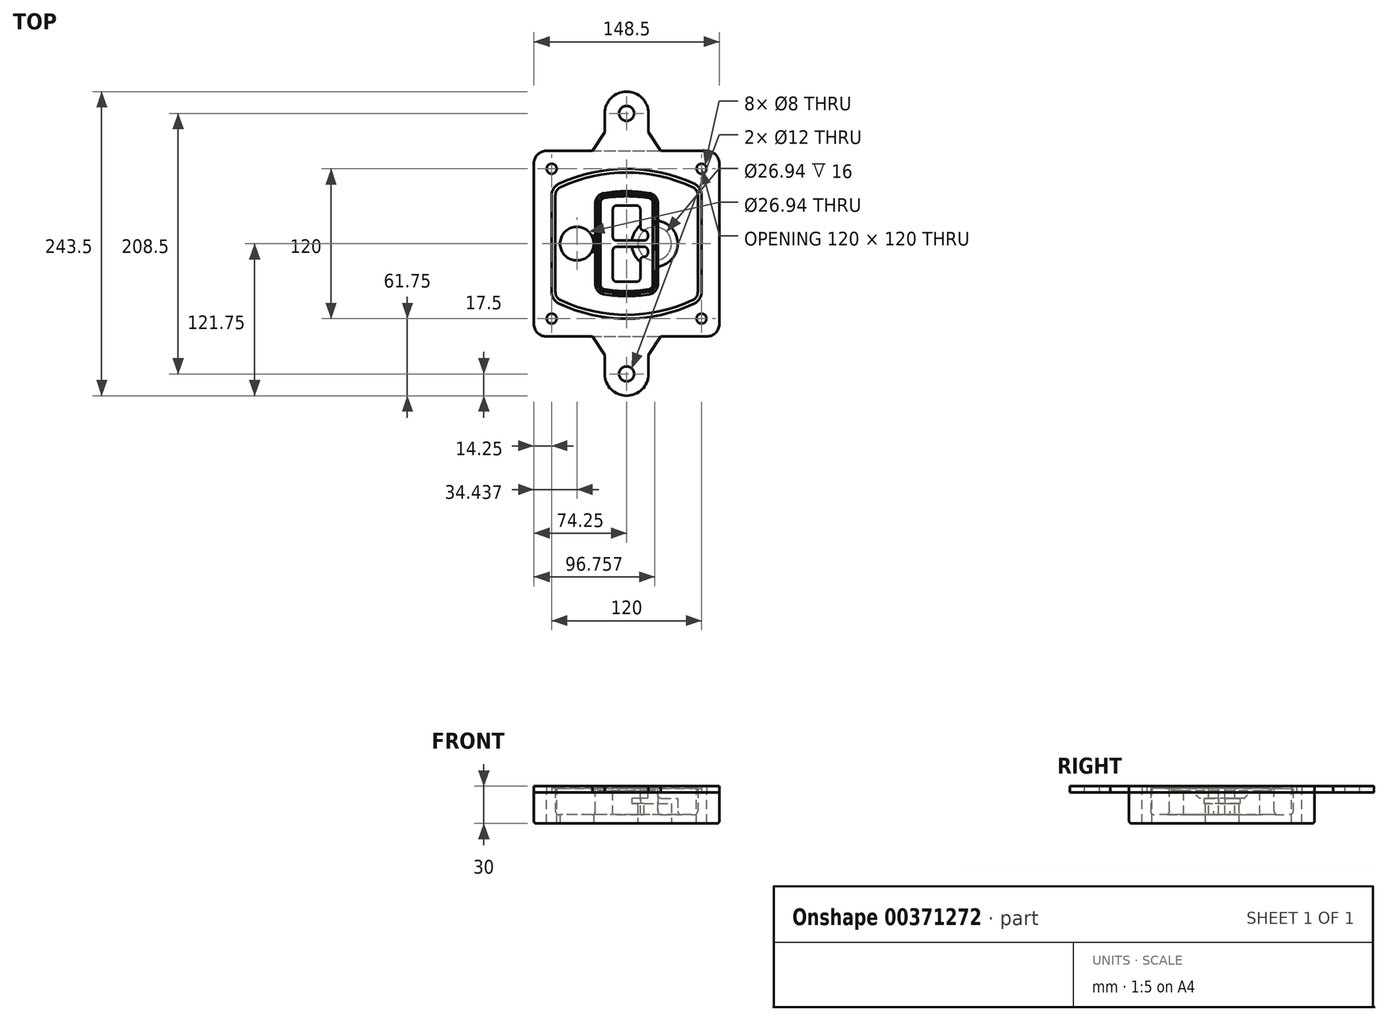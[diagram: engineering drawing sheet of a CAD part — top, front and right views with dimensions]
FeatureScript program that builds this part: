
annotation { "Feature Type Name" : "Feature", "Feature Type Description" : "" }
export const myFeature = defineFeature(function(context is Context, id is Id, definition is map)
    precondition{}
    {
        {
            var Q0;
            Q0=qCreatedBy(makeId("Top.planeOp"),FACE);
            var sketch = newSketch(context, id + "F0", { "sketchPlane" : qUnion([Q0])});
            skPoint(sketch, "E0.rect.middle", {"position": v(0, 0) * mm});
            skLineSegment(sketch, "E1.bottom", {"start": v(-64.25, -74.25) * mm, "end": v(64.25, -74.25) * mm});
            skLineSegment(sketch, "E1.top", {"start": v(-64.25, 74.25) * mm, "end": v(64.25, 74.25) * mm});
            skLineSegment(sketch, "E1.left", {"start": v(-74.25, -64.25) * mm, "end": v(-74.25, 64.25) * mm});
            skLineSegment(sketch, "E1.right", {"start": v(74.25, -64.25) * mm, "end": v(74.25, 64.25) * mm});
            skLineSegment(sketch, "E2", {"start": v(-74.25, 74.25) * mm, "end": v(74.25, -74.25) * mm, "construction": true});
            skLineSegment(sketch, "E3", {"start": v(74.25, 74.25) * mm, "end": v(-74.25, -74.25) * mm, "construction": true});
            skCircle(sketch, "E4", {"center": v(-60, 60) * mm, "radius": 4 * mm});
            skCircle(sketch, "E5", {"center": v(60, 60) * mm, "radius": 4 * mm});
            skCircle(sketch, "E6", {"center": v(60, -60) * mm, "radius": 4 * mm});
            skCircle(sketch, "E7", {"center": v(-60, -60) * mm, "radius": 4 * mm});
            skLineSegment(sketch, "E8", {"start": v(-60, 60) * mm, "end": v(60, 60) * mm, "construction": true});
            skLineSegment(sketch, "E9", {"start": v(60, 60) * mm, "end": v(60, -60) * mm, "construction": true});
            skLineSegment(sketch, "E10", {"start": v(60, -60) * mm, "end": v(-60, -60) * mm, "construction": true});
            skLineSegment(sketch, "E11", {"start": v(-60, -60) * mm, "end": v(-60, 60) * mm, "construction": true});
            skLineSegment(sketch, "E12", {"start": v(-60, 38.83) * mm, "end": v(-60, -38.83) * mm});
            skLineSegment(sketch, "E13", {"start": v(60, 38.83) * mm, "end": v(60, -38.83) * mm});
            skArc(sketch, "E14", {"start": v(54.26, 47.88) * mm, "mid": v(0, 60) * mm, "end": v(-54.26, 47.88) * mm});
            skArc(sketch, "E15", {"start": v(-54.26, -47.88) * mm, "mid": v(0, -60) * mm, "end": v(54.26, -47.88) * mm});
            skLineSegment(sketch, "E16", {"start": v(-60, 0) * mm, "end": v(60, 0) * mm, "construction": true});
            skPoint(sketch, "E17.visualSharp", {"position": v(-60, -45) * mm});
            skArc(sketch, "E17.filletArc", {"start": v(-60, -38.83) * mm, "mid": v(-58.44, -44.2) * mm, "end": v(-54.26, -47.88) * mm});
            skPoint(sketch, "E18.visualSharp", {"position": v(-60, 45) * mm});
            skArc(sketch, "E18.filletArc", {"start": v(-54.26, 47.88) * mm, "mid": v(-58.44, 44.2) * mm, "end": v(-60, 38.83) * mm});
            skPoint(sketch, "E19.visualSharp", {"position": v(60, 45) * mm});
            skArc(sketch, "E19.filletArc", {"start": v(60, 38.83) * mm, "mid": v(58.44, 44.2) * mm, "end": v(54.26, 47.88) * mm});
            skPoint(sketch, "E20.visualSharp", {"position": v(60, -45) * mm});
            skArc(sketch, "E20.filletArc", {"start": v(54.26, -47.88) * mm, "mid": v(58.44, -44.2) * mm, "end": v(60, -38.83) * mm});
            skPoint(sketch, "E21.visualSharp", {"position": v(-74.25, 74.25) * mm});
            skArc(sketch, "E21.filletArc", {"start": v(-64.25, 74.25) * mm, "mid": v(-71.32, 71.32) * mm, "end": v(-74.25, 64.25) * mm});
            skPoint(sketch, "E22.visualSharp", {"position": v(74.25, 74.25) * mm});
            skArc(sketch, "E22.filletArc", {"start": v(74.25, 64.25) * mm, "mid": v(71.32, 71.32) * mm, "end": v(64.25, 74.25) * mm});
            skPoint(sketch, "E23.visualSharp", {"position": v(74.25, -74.25) * mm});
            skArc(sketch, "E23.filletArc", {"start": v(64.25, -74.25) * mm, "mid": v(71.32, -71.32) * mm, "end": v(74.25, -64.25) * mm});
            skPoint(sketch, "E24.visualSharp", {"position": v(-74.25, -74.25) * mm});
            skArc(sketch, "E24.filletArc", {"start": v(-74.25, -64.25) * mm, "mid": v(-71.32, -71.32) * mm, "end": v(-64.25, -74.25) * mm});
            skArc(sketch, "E25.0", {"start": v(57, 38.83) * mm, "mid": v(55.9, 42.58) * mm, "end": v(52.98, 45.17) * mm});
            skLineSegment(sketch, "E25.1", {"start": v(57, 38.83) * mm, "end": v(57, -38.83) * mm});
            skArc(sketch, "E25.2", {"start": v(52.98, -45.17) * mm, "mid": v(55.9, -42.58) * mm, "end": v(57, -38.83) * mm});
            skArc(sketch, "E25.3", {"start": v(-52.98, -45.17) * mm, "mid": v(0, -57) * mm, "end": v(52.98, -45.17) * mm});
            skArc(sketch, "E25.4", {"start": v(-57, -38.83) * mm, "mid": v(-55.9, -42.58) * mm, "end": v(-52.98, -45.17) * mm});
            skArc(sketch, "E25.5", {"start": v(52.98, 45.17) * mm, "mid": v(0, 57) * mm, "end": v(-52.98, 45.17) * mm});
            skLineSegment(sketch, "E25.6", {"start": v(-57, 38.83) * mm, "end": v(-57, -38.83) * mm});
            skArc(sketch, "E25.7", {"start": v(-52.98, 45.17) * mm, "mid": v(-55.9, 42.58) * mm, "end": v(-57, 38.83) * mm});
            skArc(sketch, "E26.0", {"start": v(-55.96, 51.5) * mm, "mid": v(-61.82, 46.33) * mm, "end": v(-64, 38.83) * mm});
            skArc(sketch, "E26.1", {"start": v(55.96, 51.5) * mm, "mid": v(0, 64) * mm, "end": v(-55.96, 51.5) * mm});
            skArc(sketch, "E26.2", {"start": v(64, 38.83) * mm, "mid": v(61.82, 46.33) * mm, "end": v(55.96, 51.5) * mm});
            skLineSegment(sketch, "E26.3", {"start": v(64, 38.83) * mm, "end": v(64, -38.83) * mm});
            skArc(sketch, "E26.4", {"start": v(55.96, -51.5) * mm, "mid": v(61.82, -46.33) * mm, "end": v(64, -38.83) * mm});
            skLineSegment(sketch, "E26.5", {"start": v(-64, 38.83) * mm, "end": v(-64, -38.83) * mm});
            skArc(sketch, "E26.6", {"start": v(-55.96, -51.5) * mm, "mid": v(0, -64) * mm, "end": v(55.96, -51.5) * mm});
            skArc(sketch, "E26.7", {"start": v(-64, -38.83) * mm, "mid": v(-61.82, -46.33) * mm, "end": v(-55.96, -51.5) * mm});
            skSolve(sketch);
        }
        {
            var Q0;
            Q0=makeQuery(id+"F0.imprint","IMPRINT",FACE,{"disambiguationData":[TD([[makeQuery(id+"F0.imprint","IMPRINT",EDGE,{"derivedFrom":sQuery(id+"F0.wireOp",EDGE,"E1.bottom")}),1.0]])]});
            var Q1;
            Q1=makeQuery(id+"F0.imprint","IMPRINT",FACE,{"disambiguationData":[TD([[makeQuery(id+"F0.imprint","IMPRINT",EDGE,{"derivedFrom":sQuery(id+"F0.wireOp",EDGE,"E12")}),1.0]])]});
            var Q2;
            Q2=makeQuery(id+"F0.imprint","IMPRINT",FACE,{"disambiguationData":[TD([[makeQuery(id+"F0.imprint","IMPRINT",EDGE,{"derivedFrom":sQuery(id+"F0.wireOp",EDGE,"E25.0")}),1.0]])]});
            var Q3;
            Q3=makeQuery(id+"F0.imprint","IMPRINT",FACE,{"disambiguationData":[TD([[makeQuery(id+"F0.imprint","IMPRINT",EDGE,{"derivedFrom":sQuery(id+"F0.wireOp",EDGE,"E12")}),-1.0]])]});
            extrude(context, id + "F1", {"entities" : qUnion([Q0, Q1, Q2, Q3]), "oppositeDirection" : true, "depth" : 25 * mm});
        }
        {
            var Q0;
            Q0=makeQuery(id+"F0.imprint","IMPRINT",FACE,{"disambiguationData":[TD([[makeQuery(id+"F0.imprint","IMPRINT",EDGE,{"derivedFrom":sQuery(id+"F0.wireOp",EDGE,"E12")}),1.0]])]});
            extrude(context, id + "F2", {"entities" : qUnion([Q0]), "operationType" : NewBodyOperationType.ADD, "depth" : 3 * mm});
        }
        {
            var Q0;
            Q0=makeQuery(id+"F0.imprint","IMPRINT",FACE,{"disambiguationData":[TD([[makeQuery(id+"F0.imprint","IMPRINT",EDGE,{"derivedFrom":sQuery(id+"F0.wireOp",EDGE,"E25.0")}),1.0]])]});
            extrude(context, id + "F3", {"entities" : qUnion([Q0]), "operationType" : NewBodyOperationType.REMOVE, "oppositeDirection" : true, "depth" : 18 * mm});
        }
        {
            var Q0;
            Q0=makeQuery(id+"F2.opExtrude","CAP_FACE",FACE,{"disambiguationData":[OSD([sQuery(id+"F0.wireOp",EDGE,"E12"),sQuery(id+"F0.wireOp",EDGE,"E13"),sQuery(id+"F0.wireOp",EDGE,"E14"),sQuery(id+"F0.wireOp",EDGE,"E15"),sQuery(id+"F0.wireOp",EDGE,"E17.filletArc"),sQuery(id+"F0.wireOp",EDGE,"E18.filletArc"),sQuery(id+"F0.wireOp",EDGE,"E19.filletArc"),sQuery(id+"F0.wireOp",EDGE,"E20.filletArc"),sQuery(id+"F0.wireOp",EDGE,"E25.0"),sQuery(id+"F0.wireOp",EDGE,"E25.1"),sQuery(id+"F0.wireOp",EDGE,"E25.2"),sQuery(id+"F0.wireOp",EDGE,"E25.3"),sQuery(id+"F0.wireOp",EDGE,"E25.4"),sQuery(id+"F0.wireOp",EDGE,"E25.5"),sQuery(id+"F0.wireOp",EDGE,"E25.6"),sQuery(id+"F0.wireOp",EDGE,"E25.7")])],"isStart":false});
            var sketch = newSketch(context, id + "F4", { "sketchPlane" : qUnion([Q0])});
            skArc(sketch, "E27.0", {"start": v(-18.34, -40.45) * mm, "mid": v(0, -42) * mm, "end": v(18.34, -40.45) * mm});
            skArc(sketch, "E28.0", {"start": v(18.34, 40.45) * mm, "mid": v(0, 42) * mm, "end": v(-18.34, 40.45) * mm});
            skLineSegment(sketch, "E29", {"start": v(-25, 32.57) * mm, "end": v(-25, -32.57) * mm});
            skLineSegment(sketch, "E30", {"start": v(25, 32.57) * mm, "end": v(25, -32.57) * mm});
            skLineSegment(sketch, "E31", {"start": v(-25, 39.1) * mm, "end": v(25, 39.1) * mm, "construction": true});
            skLineSegment(sketch, "E32", {"start": v(-25, -39.1) * mm, "end": v(25, -39.1) * mm, "construction": true});
            skPoint(sketch, "E33.visualSharp", {"position": v(-25, 39.1) * mm});
            skArc(sketch, "E33.filletArc", {"start": v(-18.34, 40.45) * mm, "mid": v(-23.11, 37.73) * mm, "end": v(-25, 32.57) * mm});
            skPoint(sketch, "E34.visualSharp", {"position": v(25, 39.1) * mm});
            skArc(sketch, "E34.filletArc", {"start": v(25, 32.57) * mm, "mid": v(23.11, 37.73) * mm, "end": v(18.34, 40.45) * mm});
            skPoint(sketch, "E35.visualSharp", {"position": v(25, -39.1) * mm});
            skArc(sketch, "E35.filletArc", {"start": v(18.34, -40.45) * mm, "mid": v(23.11, -37.73) * mm, "end": v(25, -32.57) * mm});
            skPoint(sketch, "E36.visualSharp", {"position": v(-25, -39.1) * mm});
            skArc(sketch, "E36.filletArc", {"start": v(-25, -32.57) * mm, "mid": v(-23.11, -37.73) * mm, "end": v(-18.34, -40.45) * mm});
            skArc(sketch, "E37.0", {"start": v(52.98, 45.17) * mm, "mid": v(0, 57) * mm, "end": v(-52.98, 45.17) * mm});
            skArc(sketch, "E37.1", {"start": v(-52.98, 45.17) * mm, "mid": v(-55.9, 42.58) * mm, "end": v(-57, 38.83) * mm});
            skLineSegment(sketch, "E37.2", {"start": v(-57, 38.83) * mm, "end": v(-57, -38.83) * mm});
            skArc(sketch, "E37.3", {"start": v(-57, -38.83) * mm, "mid": v(-55.9, -42.58) * mm, "end": v(-52.98, -45.17) * mm});
            skArc(sketch, "E37.4", {"start": v(-52.98, -45.17) * mm, "mid": v(0, -57) * mm, "end": v(52.98, -45.17) * mm});
            skArc(sketch, "E37.5", {"start": v(52.98, -45.17) * mm, "mid": v(55.9, -42.58) * mm, "end": v(57, -38.83) * mm});
            skLineSegment(sketch, "E37.6", {"start": v(57, 38.83) * mm, "end": v(57, -38.83) * mm});
            skArc(sketch, "E37.7", {"start": v(57, 38.83) * mm, "mid": v(55.9, 42.58) * mm, "end": v(52.98, 45.17) * mm});
            skLineSegment(sketch, "E38.0", {"start": v(23, 32.57) * mm, "end": v(23, -32.57) * mm});
            skArc(sketch, "E38.1", {"start": v(18, -38.48) * mm, "mid": v(21.58, -36.44) * mm, "end": v(23, -32.57) * mm});
            skArc(sketch, "E38.2", {"start": v(-18, -38.48) * mm, "mid": v(0, -40) * mm, "end": v(18, -38.48) * mm});
            skArc(sketch, "E38.3", {"start": v(-23, -32.57) * mm, "mid": v(-21.58, -36.44) * mm, "end": v(-18, -38.48) * mm});
            skLineSegment(sketch, "E38.4", {"start": v(-23, 32.57) * mm, "end": v(-23, -32.57) * mm});
            skArc(sketch, "E38.5", {"start": v(23, 32.57) * mm, "mid": v(21.58, 36.44) * mm, "end": v(18, 38.48) * mm});
            skArc(sketch, "E38.6", {"start": v(-18, 38.48) * mm, "mid": v(-21.58, 36.44) * mm, "end": v(-23, 32.57) * mm});
            skArc(sketch, "E38.7", {"start": v(18, 38.48) * mm, "mid": v(0, 40) * mm, "end": v(-18, 38.48) * mm});
            skArc(sketch, "E39.0", {"start": v(21, 32.57) * mm, "mid": v(20.06, 35.15) * mm, "end": v(17.67, 36.5) * mm});
            skLineSegment(sketch, "E39.1", {"start": v(21, 32.57) * mm, "end": v(21, -32.57) * mm});
            skArc(sketch, "E39.2", {"start": v(17.67, -36.5) * mm, "mid": v(20.06, -35.15) * mm, "end": v(21, -32.57) * mm});
            skArc(sketch, "E39.3", {"start": v(-17.67, -36.5) * mm, "mid": v(0, -38) * mm, "end": v(17.67, -36.5) * mm});
            skArc(sketch, "E39.4", {"start": v(-21, -32.57) * mm, "mid": v(-20.06, -35.15) * mm, "end": v(-17.67, -36.5) * mm});
            skArc(sketch, "E39.5", {"start": v(17.67, 36.5) * mm, "mid": v(0, 38) * mm, "end": v(-17.67, 36.5) * mm});
            skLineSegment(sketch, "E39.6", {"start": v(-21, 32.57) * mm, "end": v(-21, -32.57) * mm});
            skArc(sketch, "E39.7", {"start": v(-17.67, 36.5) * mm, "mid": v(-20.06, 35.15) * mm, "end": v(-21, 32.57) * mm});
            skLineSegment(sketch, "E40", {"start": v(-25, 0) * mm, "end": v(25, 0) * mm, "construction": true});
            skLineSegment(sketch, "E41", {"start": v(-11, 5.5) * mm, "end": v(-11, 27.5) * mm});
            skLineSegment(sketch, "E42", {"start": v(-8, 30.5) * mm, "end": v(8, 30.5) * mm});
            skLineSegment(sketch, "E43", {"start": v(11, 27.5) * mm, "end": v(11, 13.5) * mm});
            skLineSegment(sketch, "E44", {"start": v(14, 10.5) * mm, "end": v(14, 10.5) * mm});
            skLineSegment(sketch, "E45", {"start": v(17, 7.5) * mm, "end": v(17, 5.5) * mm});
            skLineSegment(sketch, "E46", {"start": v(14, 2.5) * mm, "end": v(-8, 2.5) * mm});
            skPoint(sketch, "E47.visualSharp", {"position": v(-11, 30.5) * mm});
            skArc(sketch, "E47.filletArc", {"start": v(-8, 30.5) * mm, "mid": v(-10.12, 29.62) * mm, "end": v(-11, 27.5) * mm});
            skPoint(sketch, "E48.visualSharp", {"position": v(11, 30.5) * mm});
            skArc(sketch, "E48.filletArc", {"start": v(11, 27.5) * mm, "mid": v(10.12, 29.62) * mm, "end": v(8, 30.5) * mm});
            skPoint(sketch, "E49.visualSharp", {"position": v(11, 10.5) * mm});
            skArc(sketch, "E49.filletArc", {"start": v(11, 13.5) * mm, "mid": v(11.88, 11.38) * mm, "end": v(14, 10.5) * mm});
            skPoint(sketch, "E50.visualSharp", {"position": v(17, 10.5) * mm});
            skArc(sketch, "E50.filletArc", {"start": v(17, 7.5) * mm, "mid": v(16.12, 9.62) * mm, "end": v(14, 10.5) * mm});
            skPoint(sketch, "E51.visualSharp", {"position": v(17, 2.5) * mm});
            skArc(sketch, "E51.filletArc", {"start": v(14, 2.5) * mm, "mid": v(16.12, 3.38) * mm, "end": v(17, 5.5) * mm});
            skPoint(sketch, "E52.visualSharp", {"position": v(-11, 2.5) * mm});
            skArc(sketch, "E52.filletArc", {"start": v(-11, 5.5) * mm, "mid": v(-10.12, 3.38) * mm, "end": v(-8, 2.5) * mm});
            skLineSegment(sketch, "E53.0.MirrorCS", {"start": v(14, -2.5) * mm, "end": v(-8, -2.5) * mm});
            skArc(sketch, "E54.0.MirrorCS", {"start": v(-11, -5.5) * mm, "mid": v(-10.12, -3.38) * mm, "end": v(-8, -2.5) * mm});
            skLineSegment(sketch, "E55.0.MirrorCS", {"start": v(-11, -5.5) * mm, "end": v(-11, -27.5) * mm});
            skArc(sketch, "E56.0.MirrorCS", {"start": v(-8, -30.5) * mm, "mid": v(-10.12, -29.62) * mm, "end": v(-11, -27.5) * mm});
            skLineSegment(sketch, "E57.0.MirrorCS", {"start": v(-8, -30.5) * mm, "end": v(8, -30.5) * mm});
            skArc(sketch, "E58.0.MirrorCS", {"start": v(11, -27.5) * mm, "mid": v(10.12, -29.62) * mm, "end": v(8, -30.5) * mm});
            skLineSegment(sketch, "E59.0.MirrorCS", {"start": v(11, -27.5) * mm, "end": v(11, -13.5) * mm});
            skArc(sketch, "E60.0.MirrorCS", {"start": v(11, -13.5) * mm, "mid": v(11.88, -11.38) * mm, "end": v(14, -10.5) * mm});
            skArc(sketch, "E61.0.MirrorCS", {"start": v(17, -7.5) * mm, "mid": v(16.12, -9.62) * mm, "end": v(14, -10.5) * mm});
            skLineSegment(sketch, "E62.0.MirrorCS", {"start": v(17, -7.5) * mm, "end": v(17, -5.5) * mm});
            skArc(sketch, "E63.0.MirrorCS", {"start": v(14, -2.5) * mm, "mid": v(16.12, -3.38) * mm, "end": v(17, -5.5) * mm});
            skSolve(sketch);
        }
        {
            var Q0;
            Q0=makeQuery(id+"F4.imprint","IMPRINT",FACE,{"disambiguationData":[TD([[makeQuery(id+"F4.imprint","IMPRINT",EDGE,{"derivedFrom":sQuery(id+"F4.wireOp",EDGE,"E27.0")}),1.0]])]});
            var Q1;
            Q1=makeQuery(id+"F4.imprint","IMPRINT",FACE,{"disambiguationData":[TD([[makeQuery(id+"F4.imprint","IMPRINT",EDGE,{"derivedFrom":sQuery(id+"F4.wireOp",EDGE,"E38.0")}),-1.0]])]});
            var Q2;
            Q2=makeQuery(id+"F4.imprint","IMPRINT",FACE,{"disambiguationData":[TD([[makeQuery(id+"F4.imprint","IMPRINT",EDGE,{"derivedFrom":sQuery(id+"F4.wireOp",EDGE,"E39.0")}),1.0]])]});
            extrude(context, id + "F5", {"entities" : qUnion([Q0, Q1, Q2]), "operationType" : NewBodyOperationType.ADD, "endBound" : BoundingType.UP_TO_NEXT, "oppositeDirection" : true, "depth" : 25 * mm});
        }
        {
            var Q0;
            Q0=makeQuery(id+"F4.imprint","IMPRINT",FACE,{"disambiguationData":[TD([[makeQuery(id+"F4.imprint","IMPRINT",EDGE,{"derivedFrom":sQuery(id+"F4.wireOp",EDGE,"E38.0")}),-1.0]])]});
            extrude(context, id + "F6", {"entities" : qUnion([Q0]), "operationType" : NewBodyOperationType.REMOVE, "oppositeDirection" : true, "depth" : 2 * mm});
        }
        {
            var Q0;
            Q0=makeQuery(id+"F1.opExtrude","CAP_FACE",FACE,{"disambiguationData":[OSD([sQuery(id+"F0.wireOp",EDGE,"E1.bottom"),sQuery(id+"F0.wireOp",EDGE,"E1.top"),sQuery(id+"F0.wireOp",EDGE,"E1.left"),sQuery(id+"F0.wireOp",EDGE,"E1.right"),sQuery(id+"F0.wireOp",EDGE,"E4"),sQuery(id+"F0.wireOp",EDGE,"E5"),sQuery(id+"F0.wireOp",EDGE,"E6"),sQuery(id+"F0.wireOp",EDGE,"E7"),sQuery(id+"F0.wireOp",EDGE,"E21.filletArc"),sQuery(id+"F0.wireOp",EDGE,"E22.filletArc"),sQuery(id+"F0.wireOp",EDGE,"E23.filletArc"),sQuery(id+"F0.wireOp",EDGE,"E24.filletArc")])],"isStart":false});
            var sketch = newSketch(context, id + "F7", { "sketchPlane" : qUnion([Q0])});
            skCircle(sketch, "E64", {"center": v(22.5, 0) * mm, "radius": 13.47 * mm});
            skCircle(sketch, "E65", {"center": v(-39.81, 0) * mm, "radius": 13.47 * mm});
            skLineSegment(sketch, "E66", {"start": v(74.25, 0) * mm, "end": v(-74.25, 0) * mm});
            skCircle(sketch, "E67", {"center": v(22.5, 0) * mm, "radius": 18.47 * mm});
            skCircle(sketch, "E68", {"center": v(60, -60) * mm, "radius": 6 * mm});
            skCircle(sketch, "E69", {"center": v(-60, -60) * mm, "radius": 6 * mm});
            skCircle(sketch, "E70", {"center": v(-60, 60) * mm, "radius": 6 * mm});
            skCircle(sketch, "E71", {"center": v(60, 60) * mm, "radius": 6 * mm});
            skSolve(sketch);
        }
        {
            var Q0;
            {var subQ1=sQuery(id+"F7.wireOp",EDGE,"E66");var subQ4=sQuery(id+"F7.wireOp",EDGE,"E64");var subQ6=makeQuery(id+"F7.imprint","INTERSECT",VERTEX,{"disambiguationData":[OD(0.0)],"derivedFrom":[subQ4,subQ1]});Q0=makeQuery(id+"F7.imprint","IMPRINT",FACE,{"disambiguationData":[TD([[makeQuery(id+"F7.imprint","IMPRINT",EDGE,{"disambiguationData":[TD([[subQ6,-1.0]])],"derivedFrom":subQ4}),-1.0]])]});}
            var Q1;
            {var subQ0=sQuery(id+"F7.wireOp",EDGE,"E66");var subQ1=sQuery(id+"F7.wireOp",EDGE,"E64");var subQ3=makeQuery(id+"F7.imprint","INTERSECT",VERTEX,{"disambiguationData":[OD(0.0)],"derivedFrom":[subQ1,subQ0]});Q1=makeQuery(id+"F7.imprint","IMPRINT",FACE,{"disambiguationData":[TD([[makeQuery(id+"F7.imprint","IMPRINT",EDGE,{"disambiguationData":[TD([[subQ3,-1.0]])],"derivedFrom":subQ1}),1.0]])]});}
            var Q2;
            {var subQ0=sQuery(id+"F7.wireOp",EDGE,"E66");var subQ1=sQuery(id+"F7.wireOp",EDGE,"E64");var subQ3=makeQuery(id+"F7.imprint","INTERSECT",VERTEX,{"disambiguationData":[OD(0.0)],"derivedFrom":[subQ1,subQ0]});Q2=makeQuery(id+"F7.imprint","IMPRINT",FACE,{"disambiguationData":[TD([[makeQuery(id+"F7.imprint","IMPRINT",EDGE,{"disambiguationData":[TD([[subQ3,1.0]])],"derivedFrom":subQ1}),1.0]])]});}
            var Q3;
            {var subQ1=sQuery(id+"F7.wireOp",EDGE,"E66");var subQ4=sQuery(id+"F7.wireOp",EDGE,"E64");var subQ6=makeQuery(id+"F7.imprint","INTERSECT",VERTEX,{"disambiguationData":[OD(0.0)],"derivedFrom":[subQ4,subQ1]});Q3=makeQuery(id+"F7.imprint","IMPRINT",FACE,{"disambiguationData":[TD([[makeQuery(id+"F7.imprint","IMPRINT",EDGE,{"disambiguationData":[TD([[subQ6,1.0]])],"derivedFrom":subQ4}),-1.0]])]});}
            extrude(context, id + "F8", {"entities" : qUnion([Q0, Q1, Q2, Q3]), "operationType" : NewBodyOperationType.ADD, "oppositeDirection" : true, "depth" : 20 * mm});
        }
        {
            var Q0;
            {var subQ0=sQuery(id+"F7.wireOp",EDGE,"E66");var subQ1=sQuery(id+"F7.wireOp",EDGE,"E64");var subQ3=makeQuery(id+"F7.imprint","INTERSECT",VERTEX,{"disambiguationData":[OD(0.0)],"derivedFrom":[subQ1,subQ0]});Q0=makeQuery(id+"F7.imprint","IMPRINT",FACE,{"disambiguationData":[TD([[makeQuery(id+"F7.imprint","IMPRINT",EDGE,{"disambiguationData":[TD([[subQ3,-1.0]])],"derivedFrom":subQ1}),1.0]])]});}
            var Q1;
            {var subQ0=sQuery(id+"F7.wireOp",EDGE,"E66");var subQ1=sQuery(id+"F7.wireOp",EDGE,"E64");var subQ3=makeQuery(id+"F7.imprint","INTERSECT",VERTEX,{"disambiguationData":[OD(0.0)],"derivedFrom":[subQ1,subQ0]});Q1=makeQuery(id+"F7.imprint","IMPRINT",FACE,{"disambiguationData":[TD([[makeQuery(id+"F7.imprint","IMPRINT",EDGE,{"disambiguationData":[TD([[subQ3,1.0]])],"derivedFrom":subQ1}),1.0]])]});}
            extrude(context, id + "F9", {"entities" : qUnion([Q0, Q1]), "operationType" : NewBodyOperationType.REMOVE, "oppositeDirection" : true, "depth" : 16 * mm});
        }
        {
            var Q0;
            {var subQ0=sQuery(id+"F7.wireOp",EDGE,"E66");var subQ1=sQuery(id+"F7.wireOp",EDGE,"E65");var subQ3=makeQuery(id+"F7.imprint","INTERSECT",VERTEX,{"disambiguationData":[OD(0.0)],"derivedFrom":[subQ1,subQ0]});Q0=makeQuery(id+"F7.imprint","IMPRINT",FACE,{"disambiguationData":[TD([[makeQuery(id+"F7.imprint","IMPRINT",EDGE,{"disambiguationData":[TD([[subQ3,-1.0]])],"derivedFrom":subQ1}),1.0]])]});}
            var Q1;
            {var subQ0=sQuery(id+"F7.wireOp",EDGE,"E66");var subQ1=sQuery(id+"F7.wireOp",EDGE,"E65");var subQ3=makeQuery(id+"F7.imprint","INTERSECT",VERTEX,{"disambiguationData":[OD(0.0)],"derivedFrom":[subQ1,subQ0]});Q1=makeQuery(id+"F7.imprint","IMPRINT",FACE,{"disambiguationData":[TD([[makeQuery(id+"F7.imprint","IMPRINT",EDGE,{"disambiguationData":[TD([[subQ3,1.0]])],"derivedFrom":subQ1}),1.0]])]});}
            extrude(context, id + "F10", {"entities" : qUnion([Q0, Q1]), "operationType" : NewBodyOperationType.REMOVE, "oppositeDirection" : true, "depth" : 25 * mm});
        }
        {
            var Q0;
            Q0=makeQuery(id+"F9.boolean.opBoolean","COPY",FACE,{"derivedFrom":makeQuery(id+"F9.opExtrude","CAP_FACE",FACE,{"disambiguationData":[OSD([sQuery(id+"F7.wireOp",EDGE,"E64")])],"isStart":false})});
            var sketch = newSketch(context, id + "F11", { "sketchPlane" : qUnion([Q0])});
            skArc(sketch, "E72.0", {"start": v(11, 14.45) * mm, "mid": v(6.45, 9.13) * mm, "end": v(4.2, 2.5) * mm});
            skArc(sketch, "E72.1", {"start": v(4.2, -2.5) * mm, "mid": v(6.45, -9.13) * mm, "end": v(11, -14.45) * mm});
            skLineSegment(sketch, "E73", {"start": v(4.2, -2.5) * mm, "end": v(14, -2.5) * mm});
            skLineSegment(sketch, "E74.0", {"start": v(14, 2.5) * mm, "end": v(4.2, 2.5) * mm});
            skArc(sketch, "E74.1", {"start": v(14, 2.5) * mm, "mid": v(16.12, 3.38) * mm, "end": v(17, 5.5) * mm});
            skLineSegment(sketch, "E74.2", {"start": v(17, 7.5) * mm, "end": v(17, 5.5) * mm});
            skArc(sketch, "E74.3", {"start": v(17, 7.5) * mm, "mid": v(16.12, 9.62) * mm, "end": v(14, 10.5) * mm});
            skArc(sketch, "E74.4", {"start": v(11, 13.5) * mm, "mid": v(11.88, 11.38) * mm, "end": v(14, 10.5) * mm});
            skLineSegment(sketch, "E74.5", {"start": v(11, 14.45) * mm, "end": v(11, 13.5) * mm});
            skLineSegment(sketch, "E74.7", {"start": v(14, -2.5) * mm, "end": v(4.2, -2.5) * mm});
            skArc(sketch, "E74.8", {"start": v(14, -2.5) * mm, "mid": v(16.12, -3.38) * mm, "end": v(17, -5.5) * mm});
            skLineSegment(sketch, "E74.9", {"start": v(17, -7.5) * mm, "end": v(17, -5.5) * mm});
            skArc(sketch, "E74.10", {"start": v(17, -7.5) * mm, "mid": v(16.12, -9.62) * mm, "end": v(14, -10.5) * mm});
            skArc(sketch, "E74.11", {"start": v(11, -13.5) * mm, "mid": v(11.88, -11.38) * mm, "end": v(14, -10.5) * mm});
            skLineSegment(sketch, "E74.12", {"start": v(11, -14.45) * mm, "end": v(11, -13.5) * mm});
            skPoint(sketch, "E75.orphan", {"position": v(11, -27.5) * mm});
            skPoint(sketch, "E76.orphan", {"position": v(-8, -2.5) * mm});
            skPoint(sketch, "E77.orphan", {"position": v(-8, 2.5) * mm});
            skPoint(sketch, "E78.orphan", {"position": v(11, 27.5) * mm});
            skSolve(sketch);
        }
        {
            var Q0;
            {var subQ7=sQuery(id+"F11.wireOp",EDGE,"E72.0");var subQ14=sQuery(id+"F11.wireOp",EDGE,"E72.1");var subQ16=sQuery(id+"F11.wireOp",EDGE,"E74.1");var subQ18=sQuery(id+"F11.wireOp",EDGE,"E74.8");Q0=qUnion([makeQuery(id+"F11.imprint","IMPRINT",FACE,{"disambiguationData":[TD([[makeQuery(id+"F11.imprint","IMPRINT",EDGE,{"derivedFrom":subQ7}),1.0]])]}),makeQuery(id+"F11.imprint","IMPRINT",FACE,{"disambiguationData":[TD([[makeQuery(id+"F11.imprint","IMPRINT",EDGE,{"derivedFrom":subQ14}),1.0]])]}),makeQuery(id+"F11.imprint","IMPRINT",FACE,{"disambiguationData":[TD([[makeQuery(id+"F11.imprint","IMPRINT",EDGE,{"derivedFrom":subQ16}),1.0]])]}),makeQuery(id+"F11.imprint","IMPRINT",FACE,{"disambiguationData":[TD([[makeQuery(id+"F11.imprint","IMPRINT",EDGE,{"derivedFrom":subQ18}),-1.0]])]})]);}
            var Q1;
            Q1=makeQuery(id+"F5.boolean.opBoolean","SPLIT",FACE,{"disambiguationData":[TD([makeQuery(id+"F5.opExtrude","SWEPT_FACE",FACE,{"disambiguationData":[OSD([sQuery(id+"F4.wireOp",EDGE,"E41")])]})])],"derivedFrom":makeQuery(id+"F3.boolean.opBoolean","COPY",FACE,{"derivedFrom":makeQuery(id+"F3.opExtrude","CAP_FACE",FACE,{"disambiguationData":[OSD([sQuery(id+"F0.wireOp",EDGE,"E25.0"),sQuery(id+"F0.wireOp",EDGE,"E25.1"),sQuery(id+"F0.wireOp",EDGE,"E25.2"),sQuery(id+"F0.wireOp",EDGE,"E25.3"),sQuery(id+"F0.wireOp",EDGE,"E25.4"),sQuery(id+"F0.wireOp",EDGE,"E25.5"),sQuery(id+"F0.wireOp",EDGE,"E25.6"),sQuery(id+"F0.wireOp",EDGE,"E25.7")])],"isStart":false})})});
            extrude(context, id + "F12", {"entities" : qUnion([Q0]), "operationType" : NewBodyOperationType.REMOVE, "endBound" : BoundingType.UP_TO_SURFACE, "endBoundEntityFace" : qUnion([Q1]), "depth" : 25 * mm});
        }
        {
            var Q0;
            Q0=makeQuery(id+"F3.boolean.opBoolean","COPY",EDGE,{"derivedFrom":makeQuery(id+"F3.opExtrude","CAP_EDGE",EDGE,{"disambiguationData":[OSD([sQuery(id+"F0.wireOp",EDGE,"E25.6")])],"isStart":false})});
            var Q1;
            Q1=makeQuery(id+"F8.boolean.opBoolean","INTERSECT",EDGE,{"derivedFrom":[makeQuery(id+"F5.opExtrude","SWEPT_FACE",FACE,{"disambiguationData":[OSD([sQuery(id+"F4.wireOp",EDGE,"E30")])]}),makeQuery(id+"F8.opExtrude","CAP_FACE",FACE,{"disambiguationData":[OSD([sQuery(id+"F7.wireOp",EDGE,"E67")])],"isStart":false})]});
            var Q2;
            Q2=makeQuery(id+"F8.boolean.opBoolean","INTERSECT",EDGE,{"disambiguationData":[OD(1.0)],"derivedFrom":[makeQuery(id+"F5.opExtrude","SWEPT_FACE",FACE,{"disambiguationData":[OSD([sQuery(id+"F4.wireOp",EDGE,"E30")])]}),makeQuery(id+"F8.opExtrude","SWEPT_FACE",FACE,{"disambiguationData":[OSD([sQuery(id+"F7.wireOp",EDGE,"E67")])]})]});
            var Q3;
            {var subQ0=sQuery(id+"F4.wireOp",EDGE,"E30");Q3=makeQuery(id+"F8.boolean.opBoolean","SPLIT",EDGE,{"disambiguationData":[TD([makeQuery(id+"F5.opExtrude","SWEPT_FACE",FACE,{"disambiguationData":[OSD([sQuery(id+"F4.wireOp",EDGE,"E35.filletArc")])]})])],"derivedFrom":makeQuery(id+"F5.opExtrude","CAP_EDGE",EDGE,{"disambiguationData":[OSD([subQ0])],"isStart":false})});}
            var Q4;
            {var subQ0=sQuery(id+"F0.wireOp",EDGE,"E25.7");var subQ1=sQuery(id+"F0.wireOp",EDGE,"E25.1");var subQ2=sQuery(id+"F0.wireOp",EDGE,"E25.6");var subQ3=sQuery(id+"F0.wireOp",EDGE,"E25.5");var subQ4=sQuery(id+"F0.wireOp",EDGE,"E25.4");var subQ5=sQuery(id+"F0.wireOp",EDGE,"E25.0");var subQ6=sQuery(id+"F0.wireOp",EDGE,"E25.2");var subQ7=sQuery(id+"F0.wireOp",EDGE,"E25.3");Q4=makeQuery(id+"F8.boolean.opBoolean","INTERSECT",EDGE,{"derivedFrom":[makeQuery(id+"F5.boolean.opBoolean","SPLIT",FACE,{"disambiguationData":[TD([makeQuery(id+"F2.opExtrude","SWEPT_FACE",FACE,{"disambiguationData":[OSD([subQ5])]})])],"derivedFrom":makeQuery(id+"F3.boolean.opBoolean","COPY",FACE,{"derivedFrom":makeQuery(id+"F3.opExtrude","CAP_FACE",FACE,{"disambiguationData":[OSD([subQ5,subQ1,subQ6,subQ7,subQ4,subQ3,subQ2,subQ0])],"isStart":false})})}),makeQuery(id+"F8.opExtrude","SWEPT_FACE",FACE,{"disambiguationData":[OSD([sQuery(id+"F7.wireOp",EDGE,"E67")])]})]});}
            var Q5;
            Q5=makeQuery(id+"F8.boolean.opBoolean","INTERSECT",EDGE,{"disambiguationData":[OD(0.0)],"derivedFrom":[makeQuery(id+"F5.opExtrude","SWEPT_FACE",FACE,{"disambiguationData":[OSD([sQuery(id+"F4.wireOp",EDGE,"E30")])]}),makeQuery(id+"F8.opExtrude","SWEPT_FACE",FACE,{"disambiguationData":[OSD([sQuery(id+"F7.wireOp",EDGE,"E67")])]})]});
            fillet(context, id + "F13", {"entities" : qUnion([Q0, Q1, Q2, Q3, Q4, Q5]), "radius" : 3 * mm, "tangentPropagation" : true, "allowEdgeOverflow" : false});
        }
        {
            var Q0;
            Q0=makeQuery(id+"F1.opExtrude","CAP_EDGE",EDGE,{"disambiguationData":[OSD([sQuery(id+"F0.wireOp",EDGE,"E1.bottom")])],"isStart":false});
            fillet(context, id + "F14", {"entities" : qUnion([Q0]), "radius" : 2 * mm, "tangentPropagation" : true, "allowEdgeOverflow" : false});
        }
        {
            var Q0;
            {var subQ0=sQuery(id+"F0.wireOp",EDGE,"E21.filletArc");var subQ1=sQuery(id+"F0.wireOp",EDGE,"E7");var subQ2=sQuery(id+"F0.wireOp",EDGE,"E6");var subQ3=sQuery(id+"F0.wireOp",EDGE,"E5");var subQ4=sQuery(id+"F0.wireOp",EDGE,"E4");var subQ5=sQuery(id+"F0.wireOp",EDGE,"E22.filletArc");var subQ6=sQuery(id+"F0.wireOp",EDGE,"E1.bottom");var subQ7=sQuery(id+"F0.wireOp",EDGE,"E1.right");var subQ8=sQuery(id+"F0.wireOp",EDGE,"E1.top");var subQ9=sQuery(id+"F0.wireOp",EDGE,"E1.left");var subQ10=sQuery(id+"F0.wireOp",EDGE,"E23.filletArc");var subQ11=sQuery(id+"F0.wireOp",EDGE,"E24.filletArc");Q0=makeQuery(id+"F2.boolean.opBoolean","SPLIT",FACE,{"disambiguationData":[TD([makeQuery(id+"F1.opExtrude","SWEPT_FACE",FACE,{"disambiguationData":[OSD([subQ6])]})])],"derivedFrom":makeQuery(id+"F1.opExtrude","CAP_FACE",FACE,{"disambiguationData":[OSD([subQ6,subQ8,subQ9,subQ7,subQ4,subQ3,subQ2,subQ1,subQ0,subQ5,subQ10,subQ11])],"isStart":true})});}
            var sketch = newSketch(context, id + "F15", { "sketchPlane" : qUnion([Q0])});
            skLineSegment(sketch, "E79", {"start": v(0, 74.25) * mm, "end": v(0, 104.25) * mm, "construction": true});
            skPoint(sketch, "E79.endSnap0", {"position": v(0, 74.25) * mm});
            skCircle(sketch, "E80", {"center": v(0, 104.25) * mm, "radius": 6 * mm});
            skLineSegment(sketch, "E81", {"start": v(-27.45, 74.25) * mm, "end": v(-17.5, 89.25) * mm});
            skPoint(sketch, "E81.endSnap0", {"position": v(0, 89.25) * mm});
            skLineSegment(sketch, "E82", {"start": v(-17.5, 89.25) * mm, "end": v(-17.5, 104.25) * mm});
            skArc(sketch, "E83", {"start": v(17.5, 104.25) * mm, "mid": v(0, 121.75) * mm, "end": v(-17.5, 104.25) * mm});
            skLineSegment(sketch, "E84.MirrorCS", {"start": v(17.5, 89.25) * mm, "end": v(17.5, 104.25) * mm});
            skArc(sketch, "E85.MirrorCS", {"start": v(-17.5, 104.25) * mm, "mid": v(0, 121.75) * mm, "end": v(17.5, 104.25) * mm});
            skLineSegment(sketch, "E86.MirrorCS", {"start": v(27.45, 74.25) * mm, "end": v(17.5, 89.25) * mm});
            skLineSegment(sketch, "E87", {"start": v(-74.25, 0) * mm, "end": v(74.25, 0) * mm});
            skArc(sketch, "E88.MirrorCS", {"start": v(-17.5, -104.25) * mm, "mid": v(0, -121.75) * mm, "end": v(17.5, -104.25) * mm});
            skLineSegment(sketch, "E89.MirrorCS", {"start": v(17.5, -89.25) * mm, "end": v(17.5, -104.25) * mm});
            skLineSegment(sketch, "E90.MirrorCS", {"start": v(-17.5, -89.25) * mm, "end": v(-17.5, -104.25) * mm});
            skLineSegment(sketch, "E91.MirrorCS", {"start": v(-27.45, -74.25) * mm, "end": v(-17.5, -89.25) * mm});
            skCircle(sketch, "E92.MirrorC", {"center": v(0, -104.25) * mm, "radius": 6 * mm});
            skLineSegment(sketch, "E93.MirrorCS", {"start": v(27.45, -74.25) * mm, "end": v(17.5, -89.25) * mm});
            skLineSegment(sketch, "E94.MirrorCS", {"start": v(0, -74.25) * mm, "end": v(0, -104.25) * mm, "construction": true});
            skSolve(sketch);
        }
        {
            var Q0;
            Q0=makeQuery(id+"F15.imprint","IMPRINT",FACE,{"disambiguationData":[TD([[makeQuery(id+"F15.imprint","IMPRINT",EDGE,{"derivedFrom":sQuery(id+"F15.wireOp",EDGE,"E88.MirrorCS")}),1.0]])]});
            var Q1;
            {var subQ0=sQuery(id+"F15.wireOp",EDGE,"E81");Q1=makeQuery(id+"F15.imprint","IMPRINT",FACE,{"disambiguationData":[TD([[makeQuery(id+"F15.imprint","IMPRINT",EDGE,{"derivedFrom":subQ0}),-1.0]])]});}
            var Q2;
            Q2=makeQuery(id+"F15.imprint","IMPRINT",FACE,{"disambiguationData":[TD([[makeQuery(id+"F15.imprint","IMPRINT",EDGE,{"derivedFrom":makeQuery(id+"F1.opExtrude","CAP_EDGE",EDGE,{"disambiguationData":[OSD([sQuery(id+"F0.wireOp",EDGE,"E4")])],"isStart":true})}),-1.0]])]});
            var Q3;
            Q3=makeQuery(id+"F15.imprint","IMPRINT",FACE,{"disambiguationData":[TD([[makeQuery(id+"F15.imprint","IMPRINT",EDGE,{"derivedFrom":makeQuery(id+"F1.opExtrude","CAP_EDGE",EDGE,{"disambiguationData":[OSD([sQuery(id+"F0.wireOp",EDGE,"E6")])],"isStart":true})}),-1.0]])]});
            extrude(context, id + "F16", {"entities" : qUnion([Q0, Q1, Q2, Q3]), "depth" : 5 * mm});
        }
    });
